# Revit family: RECEPTÁCULO DE ACRÍLICO 140 X 70
name_source: partatom
category: Aparatos sanitarios
units: mm (PartAtom-declared; Revit-internal decimal feet)

## family parameters
Compartido = No
Corte con vacíos al cargar = No
Cota de conector redondo = Radio de uso
Número OmniClass = 23.45.05.14.21.11
Punto de cálculo de habitación = No
Se basa en plano de trabajo = No
Siempre vertical = Sí
Tipo de pieza = Normal
Título OmniClass = Bath/Shower Units

## types (1)
- RECEPTÁCULO DE ACRÍLICO 140 X 70
    CWFU = 1
    Cold Water Radius = 8 mm
    Elevación por defecto = 0 cm
    F_Alto = 14 cm
    F_Ancho = 70 cm
    F_Color = Blanco
    F_Descripción = Receptáculo acrílico recubierto de 2,5 mm de espesor con registro. Fibra de vidrio álcali-resistente, resina insaturada y
barra de madera MDF. Superficie interior con relieve, patas ajustables. Resiste 200 kg
    F_Peso = 15.60 kgf
    F_Productos incluidos = Desgüe gran caudal, sifón corrugado
    F_Profundidad = 140 cm
    F_SKU = SB0048901301CB
    HWFU = 1
    Receptáculo = Acrílico Recubierto
    Sanitary Radius = 20 mm
    URL = https://briggs.cl
    WFU = 2

## geometry (parser evidence)
native form markers: Sweep x3
no freeform markers — native parametric forms only
